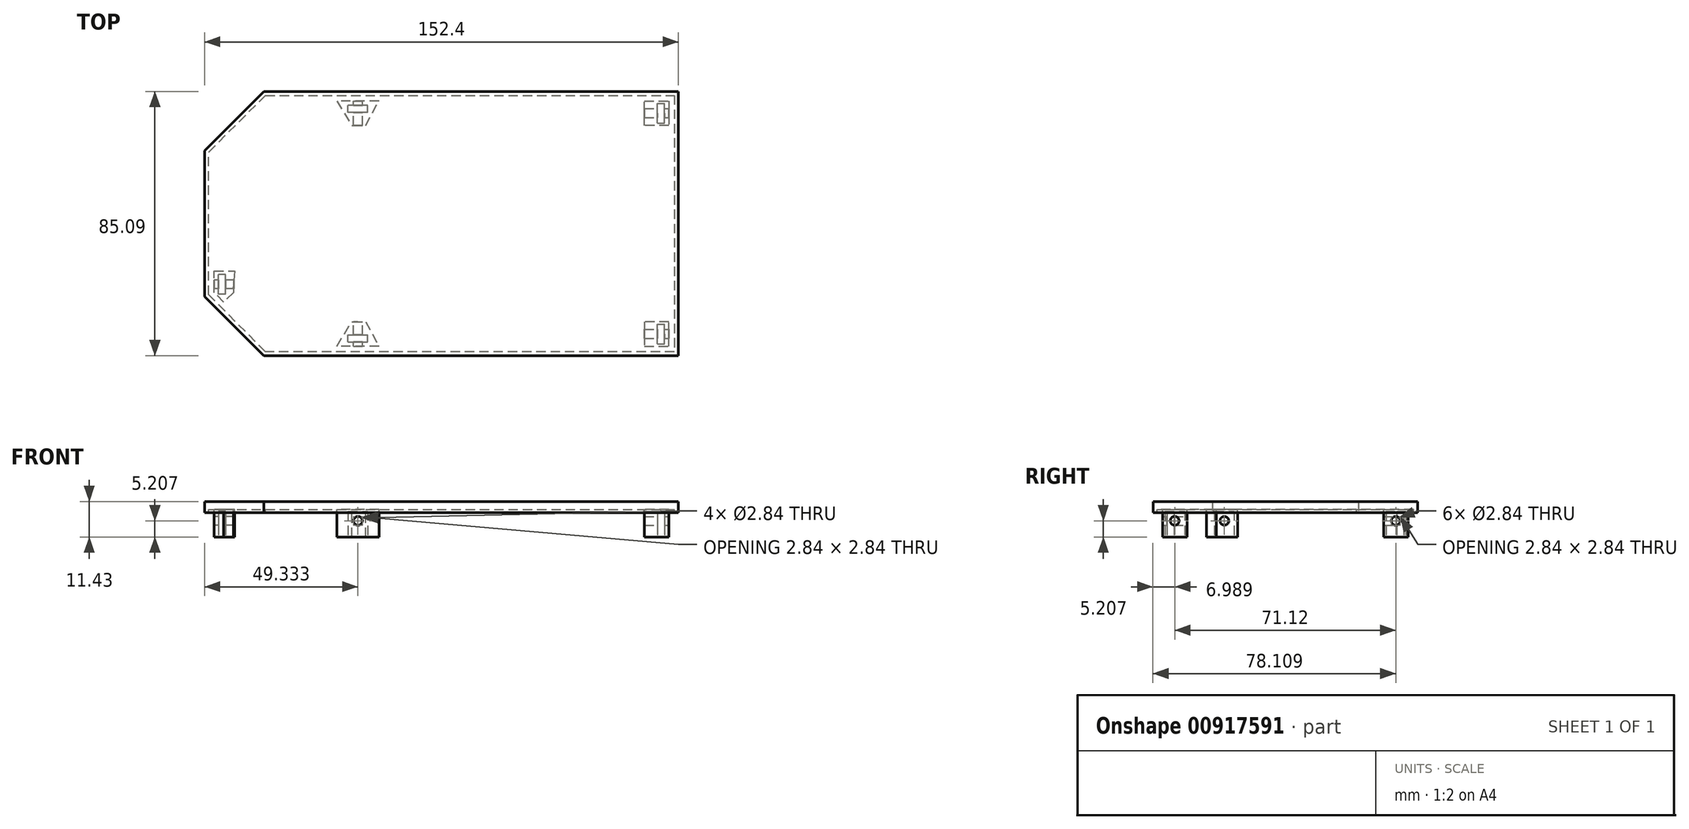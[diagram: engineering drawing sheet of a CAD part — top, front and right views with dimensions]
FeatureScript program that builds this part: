
annotation { "Feature Type Name" : "Feature", "Feature Type Description" : "" }
export const myFeature = defineFeature(function(context is Context, id is Id, definition is map)
    precondition{}
    {
        {
            var Q0;
            Q0=qCreatedBy(makeId("Top.planeOp"),FACE);
            var sketch = newSketch(context, id + "F0", { "sketchPlane" : qUnion([Q0])});
            skLineSegment(sketch, "E0", {"start": v(-68.37, -20.38) * mm, "end": v(-68.37, 25.56) * mm});
            skLineSegment(sketch, "E1", {"start": v(-68.37, 25.56) * mm, "end": v(-50.07, 43.86) * mm});
            skLineSegment(sketch, "E2", {"start": v(-50.07, 43.86) * mm, "end": v(81.49, 43.86) * mm});
            skLineSegment(sketch, "E3", {"start": v(81.49, 43.86) * mm, "end": v(81.49, -38.69) * mm});
            skLineSegment(sketch, "E4", {"start": v(81.49, -38.69) * mm, "end": v(-50.07, -38.69) * mm});
            skLineSegment(sketch, "E5", {"start": v(-50.07, -38.69) * mm, "end": v(-68.37, -20.38) * mm});
            skLineSegment(sketch, "E6", {"start": v(-61.71, -25.24) * mm, "end": v(-58.12, -21.65) * mm});
            skLineSegment(sketch, "E7", {"start": v(-58.12, -21.65) * mm, "end": v(-56.94, -12.23) * mm});
            skLineSegment(sketch, "E8", {"start": v(-56.94, -12.23) * mm, "end": v(-56.94, -9.7) * mm});
            skLineSegment(sketch, "E9", {"start": v(-56.94, -9.7) * mm, "end": v(-67.1, -9.7) * mm});
            skLineSegment(sketch, "E10", {"start": v(-67.1, -9.7) * mm, "end": v(-67.1, 25.03) * mm});
            skLineSegment(sketch, "E11", {"start": v(-67.1, 25.03) * mm, "end": v(-49.54, 42.6) * mm});
            skLineSegment(sketch, "E12", {"start": v(-49.54, 42.6) * mm, "end": v(-33.37, 42.6) * mm});
            skLineSegment(sketch, "E13", {"start": v(-19.4, 31.16) * mm, "end": v(-20.76, 31.16) * mm});
            skArc(sketch, "E14", {"start": v(-29, 40.13) * mm, "mid": v(-30.86, 41.94) * mm, "end": v(-33.37, 42.6) * mm});
            skArc(sketch, "E15", {"start": v(-25.16, 33.7) * mm, "mid": v(-23.28, 31.86) * mm, "end": v(-20.76, 31.16) * mm});
            skLineSegment(sketch, "E16", {"start": v(-25.16, 33.7) * mm, "end": v(-29, 40.13) * mm});
            skLineSegment(sketch, "E17", {"start": v(-15, 33.7) * mm, "end": v(-11.61, 39.94) * mm});
            skArc(sketch, "E18", {"start": v(-19.4, 31.16) * mm, "mid": v(-16.85, 31.85) * mm, "end": v(-15, 33.7) * mm});
            skArc(sketch, "E19", {"start": v(-7.15, 42.6) * mm, "mid": v(-9.74, 41.88) * mm, "end": v(-11.61, 39.94) * mm});
            skLineSegment(sketch, "E20", {"start": v(-7.15, 42.6) * mm, "end": v(67.52, 42.6) * mm});
            skLineSegment(sketch, "E21", {"start": v(70.06, 40.05) * mm, "end": v(70.06, 32.43) * mm});
            skLineSegment(sketch, "E22", {"start": v(70.06, 32.43) * mm, "end": v(77.68, 32.43) * mm});
            skArc(sketch, "E23", {"start": v(70.06, 40.05) * mm, "mid": v(69.31, 41.85) * mm, "end": v(67.52, 42.6) * mm});
            skArc(sketch, "E24", {"start": v(80.22, 29.9) * mm, "mid": v(79.47, 31.7) * mm, "end": v(77.68, 32.43) * mm});
            skLineSegment(sketch, "E25", {"start": v(80.22, 29.9) * mm, "end": v(80.22, -24.72) * mm});
            skArc(sketch, "E26.MirrorCS", {"start": v(80.22, -24.72) * mm, "mid": v(79.47, -26.51) * mm, "end": v(77.68, -27.26) * mm});
            skLineSegment(sketch, "E27.MirrorCS", {"start": v(70.06, -27.26) * mm, "end": v(77.68, -27.26) * mm});
            skLineSegment(sketch, "E28.MirrorCS", {"start": v(70.06, -34.88) * mm, "end": v(70.06, -27.26) * mm});
            skArc(sketch, "E29.MirrorCS", {"start": v(70.06, -34.88) * mm, "mid": v(69.31, -36.67) * mm, "end": v(67.52, -37.42) * mm});
            skLineSegment(sketch, "E30.MirrorCS", {"start": v(-7.15, -37.42) * mm, "end": v(67.52, -37.42) * mm});
            skArc(sketch, "E31.MirrorCS", {"start": v(-19.4, -25.99) * mm, "mid": v(-16.85, -26.67) * mm, "end": v(-15, -28.53) * mm});
            skArc(sketch, "E32.MirrorCS", {"start": v(-25.16, -28.53) * mm, "mid": v(-23.28, -26.69) * mm, "end": v(-20.76, -25.99) * mm});
            skLineSegment(sketch, "E33.MirrorCS", {"start": v(-19.4, -25.99) * mm, "end": v(-20.76, -25.99) * mm});
            skLineSegment(sketch, "E34.MirrorCS", {"start": v(-15, -28.53) * mm, "end": v(-11.61, -34.76) * mm});
            skArc(sketch, "E35.MirrorCS", {"start": v(-7.15, -37.42) * mm, "mid": v(-9.74, -36.7) * mm, "end": v(-11.61, -34.76) * mm});
            skLineSegment(sketch, "E36.MirrorCS", {"start": v(-25.16, -28.53) * mm, "end": v(-29, -34.95) * mm});
            skArc(sketch, "E37.MirrorCS", {"start": v(-29, -34.95) * mm, "mid": v(-30.86, -36.76) * mm, "end": v(-33.37, -37.42) * mm});
            skLineSegment(sketch, "E38.MirrorCS", {"start": v(-49.54, -37.42) * mm, "end": v(-33.37, -37.42) * mm});
            skLineSegment(sketch, "E39", {"start": v(-61.71, -25.24) * mm, "end": v(-49.54, -37.42) * mm});
            skLineSegment(sketch, "E40", {"start": v(80.22, 2.59) * mm, "end": v(-67.1, 0) * mm, "construction": true});
            skLineSegment(sketch, "E41", {"start": v(-64.17, 29.76) * mm, "end": v(-65.06, 30.66) * mm});
            skLineSegment(sketch, "E42", {"start": v(-56.22, 37.7) * mm, "end": v(-57.12, 38.6) * mm, "construction": true});
            skLineSegment(sketch, "E43", {"start": v(-38.16, 43.86) * mm, "end": v(-38.16, 45.13) * mm, "construction": true});
            skLineSegment(sketch, "E44", {"start": v(-42.74, -38.69) * mm, "end": v(-42.74, -39.96) * mm, "construction": true});
            skLineSegment(sketch, "E45", {"start": v(42.28, -38.69) * mm, "end": v(42.28, -39.96) * mm, "construction": true});
            skLineSegment(sketch, "E46", {"start": v(81.49, -17.1) * mm, "end": v(82.76, -17.1) * mm, "construction": true});
            skLineSegment(sketch, "E47", {"start": v(81.49, 14.57) * mm, "end": v(82.76, 14.57) * mm, "construction": true});
            skLineSegment(sketch, "E48", {"start": v(-55.7, -33.05) * mm, "end": v(-56.6, -33.95) * mm, "construction": true});
            skLineSegment(sketch, "E49", {"start": v(-61.8, -26.96) * mm, "end": v(-62.69, -27.86) * mm, "construction": true});
            skLineSegment(sketch, "E50", {"start": v(-42.74, -39.96) * mm, "end": v(-50.6, -39.96) * mm, "construction": true});
            skLineSegment(sketch, "E51", {"start": v(-50.6, -39.96) * mm, "end": v(82.76, -39.96) * mm});
            skLineSegment(sketch, "E52", {"start": v(82.76, -17.1) * mm, "end": v(82.76, -39.96) * mm});
            skLineSegment(sketch, "E53", {"start": v(82.76, -39.96) * mm, "end": v(82.76, 43.86) * mm});
            skLineSegment(sketch, "E54", {"start": v(-62.69, -27.86) * mm, "end": v(-50.6, -39.96) * mm});
            skLineSegment(sketch, "E55", {"start": v(-50.6, -39.96) * mm, "end": v(-69.64, -20.9) * mm});
            skLineSegment(sketch, "E56", {"start": v(-65.06, 30.66) * mm, "end": v(-50.6, 45.13) * mm});
            skLineSegment(sketch, "E57", {"start": v(-50.6, 45.13) * mm, "end": v(-69.64, 26.08) * mm});
            skLineSegment(sketch, "E58", {"start": v(-68.37, 9.51) * mm, "end": v(-69.64, 9.51) * mm, "construction": true});
            skLineSegment(sketch, "E59", {"start": v(-69.64, 9.51) * mm, "end": v(-69.64, 26.08) * mm});
            skLineSegment(sketch, "E60", {"start": v(-69.64, 26.08) * mm, "end": v(-69.64, -20.9) * mm});
            skLineSegment(sketch, "E61", {"start": v(-20.26, 43.86) * mm, "end": v(-20.26, 45.13) * mm, "construction": true});
            skLineSegment(sketch, "E62", {"start": v(33.14, 43.86) * mm, "end": v(33.14, 45.13) * mm, "construction": true});
            skLineSegment(sketch, "E63", {"start": v(33.14, 45.13) * mm, "end": v(-20.26, 45.13) * mm});
            skLineSegment(sketch, "E64", {"start": v(-20.26, 45.13) * mm, "end": v(-50.6, 45.13) * mm});
            skLineSegment(sketch, "E65", {"start": v(-50.6, 45.13) * mm, "end": v(82.76, 45.13) * mm});
            skPoint(sketch, "E65.endSnap0", {"position": v(6.44, 45.13) * mm});
            skLineSegment(sketch, "E66", {"start": v(82.76, 43.86) * mm, "end": v(82.76, 45.13) * mm});
            skPoint(sketch, "E67.orphan", {"position": v(89.1, 45.13) * mm});
            skLineSegment(sketch, "E68.0", {"start": v(-13.56, 42.09) * mm, "end": v(-27.05, 42.09) * mm});
            skLineSegment(sketch, "E68.1", {"start": v(-17.84, 34.21) * mm, "end": v(-13.56, 42.09) * mm});
            skLineSegment(sketch, "E68.2", {"start": v(-22.33, 34.21) * mm, "end": v(-17.84, 34.21) * mm});
            skLineSegment(sketch, "E68.3", {"start": v(-27.05, 42.09) * mm, "end": v(-22.33, 34.21) * mm});
            skLineSegment(sketch, "E69.0", {"start": v(-27.05, -36.9) * mm, "end": v(-22.33, -29.03) * mm});
            skLineSegment(sketch, "E69.1", {"start": v(-13.56, -36.9) * mm, "end": v(-27.05, -36.9) * mm});
            skLineSegment(sketch, "E69.2", {"start": v(-17.84, -29.03) * mm, "end": v(-13.56, -36.9) * mm});
            skLineSegment(sketch, "E69.3", {"start": v(-22.33, -29.03) * mm, "end": v(-17.84, -29.03) * mm});
            skLineSegment(sketch, "E70.0", {"start": v(-66.6, -12.74) * mm, "end": v(-60.02, -12.74) * mm});
            skLineSegment(sketch, "E70.1", {"start": v(-66.6, -19.64) * mm, "end": v(-66.6, -12.74) * mm});
            skLineSegment(sketch, "E70.2", {"start": v(-60.02, -12.74) * mm, "end": v(-60.41, -19.63) * mm});
            skLineSegment(sketch, "E70.3", {"start": v(-60.41, -19.63) * mm, "end": v(-63.5, -22.73) * mm});
            skLineSegment(sketch, "E70.4", {"start": v(-63.5, -22.73) * mm, "end": v(-66.6, -19.64) * mm});
            skLineSegment(sketch, "E71.0", {"start": v(71.84, 34.21) * mm, "end": v(71.84, 42.09) * mm});
            skLineSegment(sketch, "E71.1", {"start": v(79.71, 34.21) * mm, "end": v(71.84, 34.21) * mm});
            skLineSegment(sketch, "E71.2", {"start": v(79.71, 42.09) * mm, "end": v(79.71, 34.21) * mm});
            skLineSegment(sketch, "E71.3", {"start": v(71.84, 42.09) * mm, "end": v(79.71, 42.09) * mm});
            skLineSegment(sketch, "E72.0", {"start": v(71.84, -29.03) * mm, "end": v(71.84, -36.9) * mm});
            skLineSegment(sketch, "E72.1", {"start": v(79.71, -29.03) * mm, "end": v(71.84, -29.03) * mm});
            skLineSegment(sketch, "E72.2", {"start": v(79.71, -36.9) * mm, "end": v(79.71, -29.03) * mm});
            skLineSegment(sketch, "E72.3", {"start": v(71.84, -36.9) * mm, "end": v(79.71, -36.9) * mm});
            skSolve(sketch);
        }
        {
            var Q0;
            {var subQ6=sQuery(id+"F0.wireOp",EDGE,"E0");Q0=makeQuery(id+"F0.imprint","IMPRINT",FACE,{"disambiguationData":[TD([[makeQuery(id+"F0.imprint","IMPRINT",EDGE,{"derivedFrom":subQ6}),1.0]])]});}
            var Q1;
            Q1=makeQuery(id+"F0.imprint","IMPRINT",FACE,{"disambiguationData":[TD([[makeQuery(id+"F0.imprint","IMPRINT",EDGE,{"derivedFrom":sQuery(id+"F0.wireOp",EDGE,"9e620039-27f2-4136-bacc-bbc7736372d4.MirrorCS")}),-1.0]])]});
            var Q2;
            Q2=makeQuery(id+"F0.imprint","IMPRINT",FACE,{"disambiguationData":[TD([[makeQuery(id+"F0.imprint","IMPRINT",EDGE,{"derivedFrom":sQuery(id+"F0.wireOp",EDGE,"b43900ba-c758-4f20-92d1-66e3bbc789e1")}),-1.0]])]});
            var Q3;
            Q3=makeQuery(id+"F0.imprint","IMPRINT",FACE,{"disambiguationData":[TD([[makeQuery(id+"F0.imprint","IMPRINT",EDGE,{"derivedFrom":sQuery(id+"F0.wireOp",EDGE,"f3835e22-ec7a-4a77-9f9c-dc45f885c379")}),1.0]])]});
            var Q4;
            Q4=makeQuery(id+"F0.imprint","IMPRINT",FACE,{"disambiguationData":[TD([[makeQuery(id+"F0.imprint","IMPRINT",EDGE,{"derivedFrom":sQuery(id+"F0.wireOp",EDGE,"c71b10b8-81d4-4651-8033-13171a8276c7")}),-1.0]])]});
            var Q5;
            Q5=makeQuery(id+"F0.imprint","IMPRINT",FACE,{"disambiguationData":[TD([[makeQuery(id+"F0.imprint","IMPRINT",EDGE,{"derivedFrom":sQuery(id+"F0.wireOp",EDGE,"daf5b36f-f248-46f8-a6bc-5c628e7cbe08.MirrorCS")}),1.0]])]});
            var Q6;
            Q6=makeQuery(id+"F0.imprint","IMPRINT",FACE,{"disambiguationData":[TD([[makeQuery(id+"F0.imprint","IMPRINT",EDGE,{"derivedFrom":sQuery(id+"F0.wireOp",EDGE,"E6")}),-1.0]])]});
            var Q7;
            Q7=makeQuery(id+"F0.imprint","IMPRINT",FACE,{"disambiguationData":[TD([[makeQuery(id+"F0.imprint","IMPRINT",EDGE,{"derivedFrom":sQuery(id+"F0.wireOp",EDGE,"E68.0")}),1.0]])]});
            var Q8;
            {var subQ0=sQuery(id+"F0.wireOp",EDGE,"E0");Q8=makeQuery(id+"F0.imprint","IMPRINT",FACE,{"disambiguationData":[TD([[makeQuery(id+"F0.imprint","IMPRINT",EDGE,{"derivedFrom":subQ0}),-1.0]])]});}
            var Q9;
            Q9=makeQuery(id+"F0.imprint","IMPRINT",FACE,{"disambiguationData":[TD([[makeQuery(id+"F0.imprint","IMPRINT",EDGE,{"derivedFrom":sQuery(id+"F0.wireOp",EDGE,"E69.0")}),-1.0]])]});
            var Q10;
            Q10=makeQuery(id+"F0.imprint","IMPRINT",FACE,{"disambiguationData":[TD([[makeQuery(id+"F0.imprint","IMPRINT",EDGE,{"derivedFrom":sQuery(id+"F0.wireOp",EDGE,"E70.0")}),-1.0]])]});
            var Q11;
            Q11=makeQuery(id+"F0.imprint","IMPRINT",FACE,{"disambiguationData":[TD([[makeQuery(id+"F0.imprint","IMPRINT",EDGE,{"derivedFrom":sQuery(id+"F0.wireOp",EDGE,"E72.0")}),1.0]])]});
            var Q12;
            Q12=makeQuery(id+"F0.imprint","IMPRINT",FACE,{"disambiguationData":[TD([[makeQuery(id+"F0.imprint","IMPRINT",EDGE,{"derivedFrom":sQuery(id+"F0.wireOp",EDGE,"E71.0")}),-1.0]])]});
            extrude(context, id + "F1", {"entities" : qUnion([Q0, Q1, Q2, Q3, Q4, Q5, Q6, Q7, Q8, Q9, Q10, Q11, Q12]), "depth" : 2.54 * mm, "offsetDistance" : 25.4 * mm});
        }
        {
            var Q0;
            {var subQ6=sQuery(id+"F0.wireOp",EDGE,"E0");Q0=makeQuery(id+"F0.imprint","IMPRINT",FACE,{"disambiguationData":[TD([[makeQuery(id+"F0.imprint","IMPRINT",EDGE,{"derivedFrom":subQ6}),1.0]])]});}
            extrude(context, id + "F2", {"entities" : qUnion([Q0]), "operationType" : NewBodyOperationType.ADD, "oppositeDirection" : true, "depth" : 1.02 * mm, "offsetDistance" : 25.4 * mm});
        }
        {
            var Q0;
            Q0=makeQuery(id+"F0.imprint","IMPRINT",FACE,{"disambiguationData":[TD([[makeQuery(id+"F0.imprint","IMPRINT",EDGE,{"derivedFrom":sQuery(id+"F0.wireOp",EDGE,"E68.0")}),1.0]])]});
            var Q1;
            Q1=makeQuery(id+"F0.imprint","IMPRINT",FACE,{"disambiguationData":[TD([[makeQuery(id+"F0.imprint","IMPRINT",EDGE,{"derivedFrom":sQuery(id+"F0.wireOp",EDGE,"E69.0")}),-1.0]])]});
            var Q2;
            Q2=makeQuery(id+"F0.imprint","IMPRINT",FACE,{"disambiguationData":[TD([[makeQuery(id+"F0.imprint","IMPRINT",EDGE,{"derivedFrom":sQuery(id+"F0.wireOp",EDGE,"E70.0")}),-1.0]])]});
            var Q3;
            Q3=makeQuery(id+"F0.imprint","IMPRINT",FACE,{"disambiguationData":[TD([[makeQuery(id+"F0.imprint","IMPRINT",EDGE,{"derivedFrom":sQuery(id+"F0.wireOp",EDGE,"E72.0")}),1.0]])]});
            var Q4;
            Q4=makeQuery(id+"F0.imprint","IMPRINT",FACE,{"disambiguationData":[TD([[makeQuery(id+"F0.imprint","IMPRINT",EDGE,{"derivedFrom":sQuery(id+"F0.wireOp",EDGE,"E71.0")}),-1.0]])]});
            extrude(context, id + "F3", {"entities" : qUnion([Q0, Q1, Q2, Q3, Q4]), "operationType" : NewBodyOperationType.ADD, "oppositeDirection" : true, "depth" : 8.9 * mm, "offsetDistance" : 25.4 * mm});
        }
        {
            var Q0;
            Q0=makeQuery(id+"F3.opExtrude","CAP_FACE",FACE,{"disambiguationData":[OSD([sQuery(id+"F0.wireOp",EDGE,"E69.0"),sQuery(id+"F0.wireOp",EDGE,"E69.1"),sQuery(id+"F0.wireOp",EDGE,"E69.2"),sQuery(id+"F0.wireOp",EDGE,"E69.3")])],"isStart":false});
            var sketch = newSketch(context, id + "F4", { "sketchPlane" : qUnion([Q0])});
            skLineSegment(sketch, "E73", {"start": v(-13.56, 36.9) * mm, "end": v(-20.3, 36.9) * mm, "construction": true});
            skLineSegment(sketch, "E74", {"start": v(-20.3, 36.9) * mm, "end": v(-20.3, 34.37) * mm, "construction": true});
            skLineSegment(sketch, "E75.bottom", {"start": v(-23.48, 35.51) * mm, "end": v(-17.13, 35.51) * mm});
            skLineSegment(sketch, "E75.top", {"start": v(-23.48, 33.22) * mm, "end": v(-17.13, 33.22) * mm});
            skLineSegment(sketch, "E75.left", {"start": v(-23.48, 35.51) * mm, "end": v(-23.48, 33.22) * mm});
            skLineSegment(sketch, "E75.right", {"start": v(-17.13, 35.51) * mm, "end": v(-17.13, 33.22) * mm});
            skPoint(sketch, "E75.middle", {"position": v(-20.3, 34.37) * mm});
            skSolve(sketch);
        }
        {
            var Q0;
            Q0=makeQuery(id+"F3.opExtrude","CAP_FACE",FACE,{"disambiguationData":[OSD([sQuery(id+"F0.wireOp",EDGE,"E70.0"),sQuery(id+"F0.wireOp",EDGE,"E70.1"),sQuery(id+"F0.wireOp",EDGE,"E70.2"),sQuery(id+"F0.wireOp",EDGE,"E70.3"),sQuery(id+"F0.wireOp",EDGE,"E70.4")])],"isStart":false});
            var sketch = newSketch(context, id + "F5", { "sketchPlane" : qUnion([Q0])});
            skLineSegment(sketch, "E76", {"start": v(-66.6, 12.74) * mm, "end": v(-66.6, 16.2) * mm, "construction": true});
            skLineSegment(sketch, "E77", {"start": v(-66.6, 19.64) * mm, "end": v(-66.6, 16.2) * mm, "construction": true});
            skLineSegment(sketch, "E78", {"start": v(-66.6, 12.74) * mm, "end": v(-66.6, 17.92) * mm, "construction": true});
            skLineSegment(sketch, "E79", {"start": v(-66.6, 16.99) * mm, "end": v(-64.05, 16.99) * mm, "construction": true});
            skLineSegment(sketch, "E80.bottom", {"start": v(-62.91, 20.16) * mm, "end": v(-65.2, 20.16) * mm});
            skLineSegment(sketch, "E80.top", {"start": v(-62.91, 13.81) * mm, "end": v(-65.2, 13.81) * mm});
            skLineSegment(sketch, "E80.left", {"start": v(-62.91, 20.16) * mm, "end": v(-62.91, 13.81) * mm});
            skLineSegment(sketch, "E80.right", {"start": v(-65.2, 20.16) * mm, "end": v(-65.2, 13.81) * mm});
            skPoint(sketch, "E80.middle", {"position": v(-64.05, 16.99) * mm});
            skSolve(sketch);
        }
        {
            var Q0;
            Q0=makeQuery(id+"F3.opExtrude","CAP_FACE",FACE,{"disambiguationData":[OSD([sQuery(id+"F0.wireOp",EDGE,"E68.0"),sQuery(id+"F0.wireOp",EDGE,"E68.1"),sQuery(id+"F0.wireOp",EDGE,"E68.2"),sQuery(id+"F0.wireOp",EDGE,"E68.3")])],"isStart":false});
            var sketch = newSketch(context, id + "F6", { "sketchPlane" : qUnion([Q0])});
            skLineSegment(sketch, "E81", {"start": v(-27.05, -42.09) * mm, "end": v(-20.3, -42.09) * mm, "construction": true});
            skLineSegment(sketch, "E82", {"start": v(-20.3, -42.09) * mm, "end": v(-20.3, -39.55) * mm, "construction": true});
            skLineSegment(sketch, "E83.bottom", {"start": v(-17.13, -38.4) * mm, "end": v(-23.48, -38.4) * mm});
            skLineSegment(sketch, "E83.top", {"start": v(-17.13, -40.69) * mm, "end": v(-23.48, -40.69) * mm});
            skLineSegment(sketch, "E83.left", {"start": v(-17.13, -38.4) * mm, "end": v(-17.13, -40.69) * mm});
            skLineSegment(sketch, "E83.right", {"start": v(-23.48, -38.4) * mm, "end": v(-23.48, -40.69) * mm});
            skPoint(sketch, "E83.middle", {"position": v(-20.3, -39.55) * mm});
            skSolve(sketch);
        }
        {
            var Q0;
            Q0=makeQuery(id+"F3.opExtrude","CAP_FACE",FACE,{"disambiguationData":[OSD([sQuery(id+"F0.wireOp",EDGE,"E72.0"),sQuery(id+"F0.wireOp",EDGE,"E72.1"),sQuery(id+"F0.wireOp",EDGE,"E72.2"),sQuery(id+"F0.wireOp",EDGE,"E72.3")])],"isStart":false});
            var sketch = newSketch(context, id + "F7", { "sketchPlane" : qUnion([Q0])});
            skLineSegment(sketch, "E84", {"start": v(79.71, 32.97) * mm, "end": v(77.17, 32.97) * mm, "construction": true});
            skLineSegment(sketch, "E85.bottom", {"start": v(76.03, 36.15) * mm, "end": v(78.31, 36.15) * mm});
            skLineSegment(sketch, "E85.top", {"start": v(76.03, 29.8) * mm, "end": v(78.31, 29.8) * mm});
            skLineSegment(sketch, "E85.left", {"start": v(76.03, 36.15) * mm, "end": v(76.03, 29.8) * mm});
            skLineSegment(sketch, "E85.right", {"start": v(78.31, 36.15) * mm, "end": v(78.31, 29.8) * mm});
            skPoint(sketch, "E85.middle", {"position": v(77.17, 32.97) * mm});
            skSolve(sketch);
        }
        {
            var Q0;
            Q0=makeQuery(id+"F3.opExtrude","CAP_FACE",FACE,{"disambiguationData":[OSD([sQuery(id+"F0.wireOp",EDGE,"E71.0"),sQuery(id+"F0.wireOp",EDGE,"E71.1"),sQuery(id+"F0.wireOp",EDGE,"E71.2"),sQuery(id+"F0.wireOp",EDGE,"E71.3")])],"isStart":false});
            var sketch = newSketch(context, id + "F8", { "sketchPlane" : qUnion([Q0])});
            skLineSegment(sketch, "E86", {"start": v(79.71, -38.15) * mm, "end": v(77.17, -38.15) * mm, "construction": true});
            skLineSegment(sketch, "E87.bottom", {"start": v(76.03, -34.97) * mm, "end": v(78.31, -34.97) * mm});
            skLineSegment(sketch, "E87.top", {"start": v(76.03, -41.32) * mm, "end": v(78.31, -41.32) * mm});
            skLineSegment(sketch, "E87.left", {"start": v(76.03, -34.97) * mm, "end": v(76.03, -41.32) * mm});
            skLineSegment(sketch, "E87.right", {"start": v(78.31, -34.97) * mm, "end": v(78.31, -41.32) * mm});
            skPoint(sketch, "E87.middle", {"position": v(77.17, -38.15) * mm});
            skSolve(sketch);
        }
        {
            var Q0;
            Q0=makeQuery(id+"F8.imprint","IMPRINT",FACE,{"disambiguationData":[TD([[makeQuery(id+"F8.imprint","IMPRINT",EDGE,{"derivedFrom":sQuery(id+"F8.wireOp",EDGE,"E87.bottom")}),-1.0]])]});
            var Q1;
            Q1=makeQuery(id+"F7.imprint","IMPRINT",FACE,{"disambiguationData":[TD([[makeQuery(id+"F7.imprint","IMPRINT",EDGE,{"derivedFrom":sQuery(id+"F7.wireOp",EDGE,"E85.bottom")}),-1.0]])]});
            var Q2;
            Q2=makeQuery(id+"F4.imprint","IMPRINT",FACE,{"disambiguationData":[TD([[makeQuery(id+"F4.imprint","IMPRINT",EDGE,{"derivedFrom":sQuery(id+"F4.wireOp",EDGE,"E75.bottom")}),-1.0]])]});
            var Q3;
            Q3=makeQuery(id+"F5.imprint","IMPRINT",FACE,{"disambiguationData":[TD([[makeQuery(id+"F5.imprint","IMPRINT",EDGE,{"derivedFrom":sQuery(id+"F5.wireOp",EDGE,"E80.bottom")}),1.0]])]});
            var Q4;
            Q4=makeQuery(id+"F6.imprint","IMPRINT",FACE,{"disambiguationData":[TD([[makeQuery(id+"F6.imprint","IMPRINT",EDGE,{"derivedFrom":sQuery(id+"F6.wireOp",EDGE,"E83.bottom")}),1.0]])]});
            extrude(context, id + "F9", {"entities" : qUnion([Q0, Q1, Q2, Q3, Q4]), "operationType" : NewBodyOperationType.REMOVE, "oppositeDirection" : true, "depth" : 8.25 * mm, "offsetDistance" : 25.4 * mm});
        }
        {
            var Q0;
            Q0=makeQuery(id+"F3.opExtrude","SWEPT_FACE",FACE,{"disambiguationData":[OSD([sQuery(id+"F0.wireOp",EDGE,"E68.0")])]});
            var sketch = newSketch(context, id + "F10", { "sketchPlane" : qUnion([Q0])});
            skLineSegment(sketch, "E88", {"start": v(27.05, 0) * mm, "end": v(20.3, 0) * mm, "construction": true});
            skLineSegment(sketch, "E89", {"start": v(20.3, 0) * mm, "end": v(20.3, -3.68) * mm, "construction": true});
            skCircle(sketch, "E90", {"center": v(20.3, -3.68) * mm, "radius": 1.42 * mm});
            skSolve(sketch);
        }
        {
            var Q0;
            Q0=makeQuery(id+"F10.imprint","IMPRINT",FACE,{"disambiguationData":[TD([[makeQuery(id+"F10.imprint","IMPRINT",EDGE,{"derivedFrom":sQuery(id+"F10.wireOp",EDGE,"E90")}),1.0]])]});
            extrude(context, id + "F11", {"entities" : qUnion([Q0]), "operationType" : NewBodyOperationType.REMOVE, "oppositeDirection" : true, "depth" : 101.6 * mm, "offsetDistance" : 25.4 * mm});
        }
        {
            var Q0;
            Q0=makeQuery(id+"F3.opExtrude","SWEPT_FACE",FACE,{"disambiguationData":[OSD([sQuery(id+"F0.wireOp",EDGE,"E71.2")])]});
            var sketch = newSketch(context, id + "F12", { "sketchPlane" : qUnion([Q0])});
            skLineSegment(sketch, "E91", {"start": v(38.15, 0) * mm, "end": v(38.15, -3.68) * mm, "construction": true});
            skCircle(sketch, "E92", {"center": v(38.15, -3.68) * mm, "radius": 1.42 * mm});
            skSolve(sketch);
        }
        {
            var Q0;
            Q0=makeQuery(id+"F3.opExtrude","SWEPT_FACE",FACE,{"disambiguationData":[OSD([sQuery(id+"F0.wireOp",EDGE,"E72.2")])]});
            var sketch = newSketch(context, id + "F13", { "sketchPlane" : qUnion([Q0])});
            skLineSegment(sketch, "E93", {"start": v(-32.97, 0) * mm, "end": v(-32.97, -3.68) * mm, "construction": true});
            skCircle(sketch, "E94", {"center": v(-32.97, -3.68) * mm, "radius": 1.42 * mm});
            skSolve(sketch);
        }
        {
            var Q0;
            Q0=makeQuery(id+"F12.imprint","IMPRINT",FACE,{"disambiguationData":[TD([[makeQuery(id+"F12.imprint","IMPRINT",EDGE,{"derivedFrom":sQuery(id+"F12.wireOp",EDGE,"E92")}),1.0]])]});
            var Q1;
            Q1=makeQuery(id+"F13.imprint","IMPRINT",FACE,{"disambiguationData":[TD([[makeQuery(id+"F13.imprint","IMPRINT",EDGE,{"derivedFrom":sQuery(id+"F13.wireOp",EDGE,"E94")}),1.0]])]});
            extrude(context, id + "F14", {"entities" : qUnion([Q0, Q1]), "operationType" : NewBodyOperationType.REMOVE, "oppositeDirection" : true, "depth" : 25.4 * mm, "offsetDistance" : 25.4 * mm});
        }
        {
            var Q0;
            Q0=makeQuery(id+"F3.opExtrude","SWEPT_FACE",FACE,{"disambiguationData":[OSD([sQuery(id+"F0.wireOp",EDGE,"E70.1")])]});
            var sketch = newSketch(context, id + "F15", { "sketchPlane" : qUnion([Q0])});
            skLineSegment(sketch, "E95", {"start": v(12.74, 0) * mm, "end": v(16.98, 0) * mm, "construction": true});
            skLineSegment(sketch, "E96", {"start": v(16.98, 0) * mm, "end": v(16.98, -3.68) * mm, "construction": true});
            skCircle(sketch, "E97", {"center": v(16.98, -3.68) * mm, "radius": 1.42 * mm});
            skSolve(sketch);
        }
        {
            var Q0;
            Q0=makeQuery(id+"F15.imprint","IMPRINT",FACE,{"disambiguationData":[TD([[makeQuery(id+"F15.imprint","IMPRINT",EDGE,{"derivedFrom":sQuery(id+"F15.wireOp",EDGE,"E97")}),1.0]])]});
            extrude(context, id + "F16", {"entities" : qUnion([Q0]), "operationType" : NewBodyOperationType.REMOVE, "oppositeDirection" : true, "depth" : 25.4 * mm, "offsetDistance" : 25.4 * mm});
        }
    });
